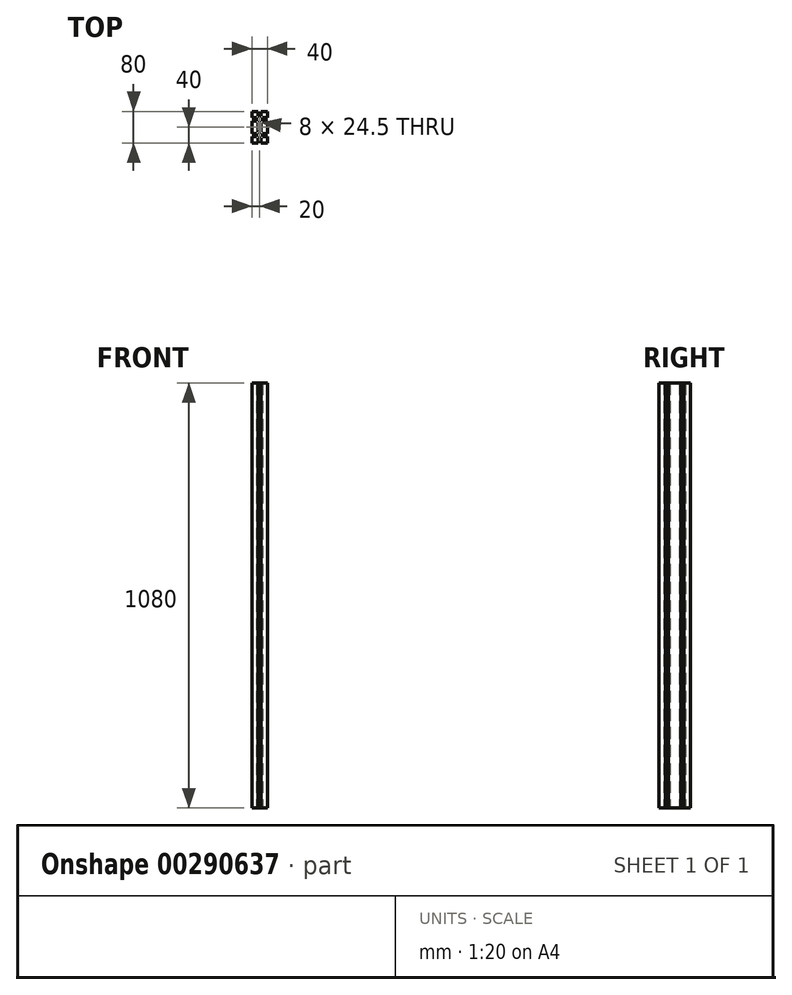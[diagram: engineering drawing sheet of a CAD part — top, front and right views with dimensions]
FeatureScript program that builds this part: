
annotation { "Feature Type Name" : "Feature", "Feature Type Description" : "" }
export const myFeature = defineFeature(function(context is Context, id is Id, definition is map)
    precondition{}
    {
        {
            var Q0;
            Q0=qCreatedBy(makeId("Top.planeOp"),FACE);
            var sketch = newSketch(context, id + "F0", { "sketchPlane" : qUnion([Q0])});
            skLineSegment(sketch, "E0.bottom", {"start": v(0, 0) * mm, "end": v(16, 0) * mm});
            skLineSegment(sketch, "E0.top", {"start": v(0, 40) * mm, "end": v(40, 40) * mm});
            skLineSegment(sketch, "E0.left", {"start": v(0, 0) * mm, "end": v(0, 40) * mm});
            skLineSegment(sketch, "E0.right", {"start": v(40, 0) * mm, "end": v(40, 40) * mm});
            skLineSegment(sketch, "E1.bottom", {"start": v(16, 40) * mm, "end": v(24, 40) * mm});
            skLineSegment(sketch, "E1.top", {"start": v(16, 27.75) * mm, "end": v(24, 27.75) * mm});
            skLineSegment(sketch, "E1.left", {"start": v(16, 40) * mm, "end": v(16, 27.75) * mm});
            skLineSegment(sketch, "E1.right", {"start": v(24, 40) * mm, "end": v(24, 27.75) * mm});
            skLineSegment(sketch, "E2.bottom", {"start": v(40, 24) * mm, "end": v(27.75, 24) * mm});
            skLineSegment(sketch, "E2.top", {"start": v(40, 16) * mm, "end": v(27.75, 16) * mm});
            skLineSegment(sketch, "E2.left", {"start": v(40, 24) * mm, "end": v(40, 16) * mm});
            skLineSegment(sketch, "E2.right", {"start": v(27.75, 24) * mm, "end": v(27.75, 16) * mm});
            skLineSegment(sketch, "E3.top", {"start": v(24, 12.25) * mm, "end": v(16, 12.25) * mm});
            skLineSegment(sketch, "E3.left", {"start": v(24, 0) * mm, "end": v(24, 12.25) * mm});
            skLineSegment(sketch, "E3.right", {"start": v(16, 0) * mm, "end": v(16, 12.25) * mm});
            skLineSegment(sketch, "E4.bottom", {"start": v(0, 16) * mm, "end": v(12.25, 16) * mm});
            skLineSegment(sketch, "E4.top", {"start": v(0, 24) * mm, "end": v(12.25, 24) * mm});
            skLineSegment(sketch, "E4.left", {"start": v(0, 16) * mm, "end": v(0, 24) * mm});
            skLineSegment(sketch, "E4.right", {"start": v(12.25, 16) * mm, "end": v(12.25, 24) * mm});
            skLineSegment(sketch, "E5.MirrorCS", {"start": v(12.25, -16) * mm, "end": v(12.25, -24) * mm});
            skLineSegment(sketch, "E6.MirrorCS", {"start": v(24, -12.25) * mm, "end": v(16, -12.25) * mm});
            skLineSegment(sketch, "E7.MirrorCS", {"start": v(0, -40) * mm, "end": v(40, -40) * mm});
            skLineSegment(sketch, "E8.MirrorCS", {"start": v(16, -40) * mm, "end": v(24, -40) * mm});
            skLineSegment(sketch, "E9.MirrorCS", {"start": v(16, -27.75) * mm, "end": v(24, -27.75) * mm});
            skLineSegment(sketch, "E10.MirrorCS", {"start": v(16, -40) * mm, "end": v(16, -27.75) * mm});
            skLineSegment(sketch, "E11.MirrorCS", {"start": v(24, -40) * mm, "end": v(24, -27.75) * mm});
            skLineSegment(sketch, "E12.MirrorCS", {"start": v(40, -24) * mm, "end": v(27.75, -24) * mm});
            skLineSegment(sketch, "E13.MirrorCS", {"start": v(40, -16) * mm, "end": v(27.75, -16) * mm});
            skLineSegment(sketch, "E14.MirrorCS", {"start": v(40, -24) * mm, "end": v(40, -16) * mm});
            skLineSegment(sketch, "E15.MirrorCS", {"start": v(27.75, -24) * mm, "end": v(27.75, -16) * mm});
            skLineSegment(sketch, "E16.MirrorCS", {"start": v(0, -16) * mm, "end": v(12.25, -16) * mm});
            skLineSegment(sketch, "E17.MirrorCS", {"start": v(0, -24) * mm, "end": v(12.25, -24) * mm});
            skLineSegment(sketch, "E18.MirrorCS", {"start": v(0, -16) * mm, "end": v(0, -24) * mm});
            skLineSegment(sketch, "E19.MirrorCS", {"start": v(16, 0) * mm, "end": v(16, -12.25) * mm});
            skLineSegment(sketch, "E20.MirrorCS", {"start": v(40, 0) * mm, "end": v(40, -40) * mm});
            skLineSegment(sketch, "E21.MirrorCS", {"start": v(0, 0) * mm, "end": v(0, -40) * mm});
            skLineSegment(sketch, "E22.MirrorCS", {"start": v(24, 0) * mm, "end": v(24, -12.25) * mm});
            skLineSegment(sketch, "E23.trimOffspring", {"start": v(24, 0) * mm, "end": v(40, 0) * mm});
            skSolve(sketch);
        }
        {
            var Q0;
            Q0=makeQuery(id+"F0.imprint","IMPRINT",FACE,{"disambiguationData":[TD([[makeQuery(id+"F0.imprint","IMPRINT",EDGE,{"derivedFrom":sQuery(id+"F0.wireOp",EDGE,"E1.top")}),-1.0]])]});
            var Q1;
            {var subQ8=sQuery(id+"F0.wireOp",EDGE,"E0.bottom");Q1=makeQuery(id+"F0.imprint","IMPRINT",FACE,{"disambiguationData":[TD([[makeQuery(id+"F0.imprint","IMPRINT",EDGE,{"derivedFrom":subQ8}),-1.0]])]});}
            extrude(context, id + "F1", {"entities" : qUnion([Q0, Q1]), "depth" : 1080 * mm});
        }
    });
